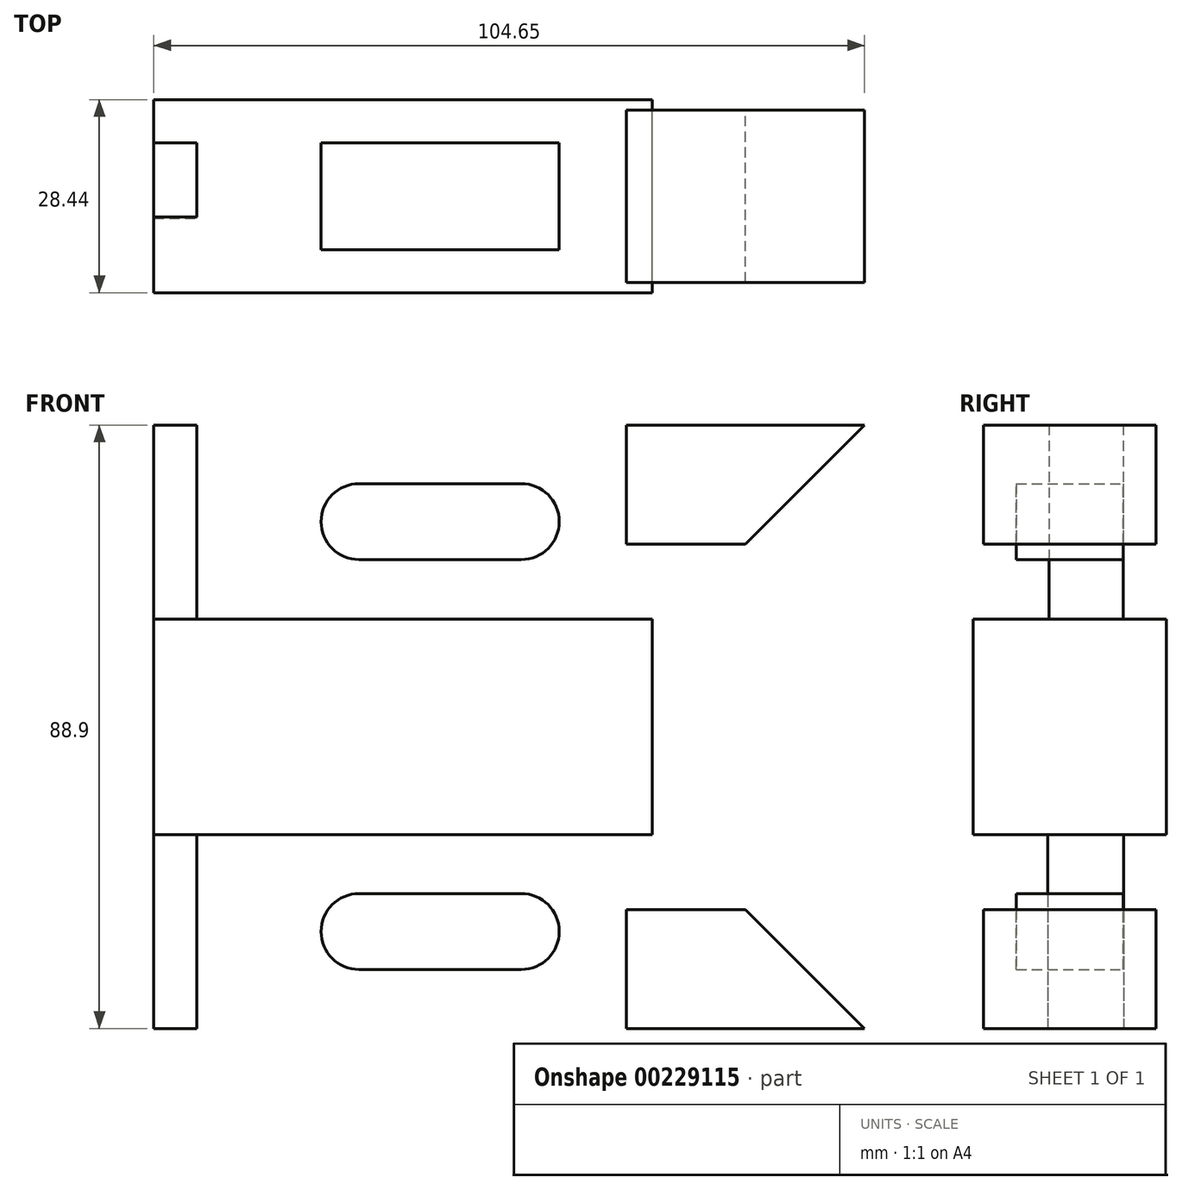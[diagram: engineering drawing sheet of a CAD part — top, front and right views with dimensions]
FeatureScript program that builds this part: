
annotation { "Feature Type Name" : "Feature", "Feature Type Description" : "" }
export const myFeature = defineFeature(function(context is Context, id is Id, definition is map)
    precondition{}
    {
        {
            var Q0;
            Q0=qCreatedBy(makeId("Front.planeOp"),FACE);
            var sketch = newSketch(context, id + "F0", { "sketchPlane" : qUnion([Q0])});
            skLineSegment(sketch, "E0.bottom", {"start": v(0, 0) * mm, "end": v(-104.65, 0) * mm});
            skLineSegment(sketch, "E0.top", {"start": v(0, 28.57) * mm, "end": v(-104.65, 28.57) * mm});
            skLineSegment(sketch, "E0.right", {"start": v(-104.65, 0) * mm, "end": v(-104.65, 28.58) * mm});
            skLineSegment(sketch, "E1", {"start": v(-74.42, 14.35) * mm, "end": v(-50.55, 14.35) * mm, "construction": true});
            skArc(sketch, "E2.0.startCap", {"start": v(-74.42, 8.76) * mm, "mid": v(-80, 14.35) * mm, "end": v(-74.42, 19.94) * mm});
            skArc(sketch, "E2.0.endCap", {"start": v(-50.55, 19.94) * mm, "mid": v(-44.96, 14.35) * mm, "end": v(-50.55, 8.76) * mm});
            skLineSegment(sketch, "E2.0.left", {"start": v(-74.42, 19.94) * mm, "end": v(-50.55, 19.94) * mm});
            skLineSegment(sketch, "E2.0.right", {"start": v(-74.42, 8.76) * mm, "end": v(-50.55, 8.76) * mm});
            skLineSegment(sketch, "E3.bottom", {"start": v(-104.65, 0) * mm, "end": v(-31.24, 0) * mm});
            skLineSegment(sketch, "E3.top", {"start": v(-104.65, -31.75) * mm, "end": v(-31.24, -31.75) * mm});
            skLineSegment(sketch, "E3.left", {"start": v(-104.65, 0) * mm, "end": v(-104.65, -31.75) * mm});
            skLineSegment(sketch, "E3.right", {"start": v(-31.24, 0) * mm, "end": v(-31.24, -31.75) * mm});
            skLineSegment(sketch, "E4.top", {"start": v(-104.65, -60.32) * mm, "end": v(0, -60.33) * mm});
            skLineSegment(sketch, "E4.left", {"start": v(-104.65, -31.75) * mm, "end": v(-104.65, -60.32) * mm});
            skLineSegment(sketch, "E5", {"start": v(-74.42, -46.04) * mm, "end": v(-50.55, -46.04) * mm, "construction": true});
            skPoint(sketch, "E5.startSnap0", {"position": v(-104.65, -46.04) * mm});
            skArc(sketch, "E6.0.startCap", {"start": v(-74.42, -51.63) * mm, "mid": v(-80, -46.04) * mm, "end": v(-74.42, -40.45) * mm});
            skArc(sketch, "E6.0.endCap", {"start": v(-50.55, -40.45) * mm, "mid": v(-44.96, -46.04) * mm, "end": v(-50.55, -51.63) * mm});
            skLineSegment(sketch, "E6.0.left", {"start": v(-74.42, -40.45) * mm, "end": v(-50.55, -40.45) * mm});
            skLineSegment(sketch, "E6.0.right", {"start": v(-74.42, -51.63) * mm, "end": v(-50.55, -51.63) * mm});
            skLineSegment(sketch, "E7", {"start": v(0, -60.32) * mm, "end": v(-28.58, -31.75) * mm});
            skLineSegment(sketch, "E8", {"start": v(0, 28.57) * mm, "end": v(-28.57, 0) * mm});
            skLineSegment(sketch, "E9", {"start": v(-31.24, 0) * mm, "end": v(-28.57, 0) * mm});
            skLineSegment(sketch, "E10", {"start": v(-31.24, -31.75) * mm, "end": v(-28.58, -31.75) * mm});
            skLineSegment(sketch, "E11", {"start": v(-98.3, 28.58) * mm, "end": v(-98.3, 0) * mm});
            skLineSegment(sketch, "E12", {"start": v(-98.3, -31.75) * mm, "end": v(-98.3, -60.32) * mm});
            skLineSegment(sketch, "E13", {"start": v(-35.05, 28.58) * mm, "end": v(-35.05, 11.05) * mm});
            skLineSegment(sketch, "E14", {"start": v(-35.05, 11.05) * mm, "end": v(-17.53, 11.05) * mm});
            skLineSegment(sketch, "E15", {"start": v(-35.05, -60.33) * mm, "end": v(-35.05, -42.8) * mm});
            skLineSegment(sketch, "E16", {"start": v(-35.05, -42.8) * mm, "end": v(-17.53, -42.8) * mm});
            skSolve(sketch);
        }
        {
            var Q0;
            {var subQ1=sQuery(id+"F0.wireOp",EDGE,"E3.left");Q0=makeQuery(id+"F0.imprint","IMPRINT",FACE,{"disambiguationData":[TD([[makeQuery(id+"F0.imprint","IMPRINT",EDGE,{"derivedFrom":subQ1}),1.0]])]});}
            extrude(context, id + "F1", {"entities" : qUnion([Q0]), "endBound" : BoundingType.SYMMETRIC, "depth" : 28.45 * mm});
        }
        {
            var Q0;
            {var subQ3=sQuery(id+"F0.wireOp",EDGE,"E13");Q0=makeQuery(id+"F0.imprint","IMPRINT",FACE,{"disambiguationData":[TD([[makeQuery(id+"F0.imprint","IMPRINT",EDGE,{"derivedFrom":subQ3}),1.0]])]});}
            var Q1;
            {var subQ3=sQuery(id+"F0.wireOp",EDGE,"E15");Q1=makeQuery(id+"F0.imprint","IMPRINT",FACE,{"disambiguationData":[TD([[makeQuery(id+"F0.imprint","IMPRINT",EDGE,{"derivedFrom":subQ3}),-1.0]])]});}
            extrude(context, id + "F2", {"entities" : qUnion([Q0, Q1]), "endBound" : BoundingType.SYMMETRIC, "depth" : 25.4 * mm});
        }
        {
            var Q0;
            Q0=makeQuery(id+"F0.imprint","IMPRINT",FACE,{"disambiguationData":[TD([[makeQuery(id+"F0.imprint","IMPRINT",EDGE,{"derivedFrom":sQuery(id+"F0.wireOp",EDGE,"E2.0.startCap")}),1.0]])]});
            var Q1;
            Q1=makeQuery(id+"F0.imprint","IMPRINT",FACE,{"disambiguationData":[TD([[makeQuery(id+"F0.imprint","IMPRINT",EDGE,{"derivedFrom":sQuery(id+"F0.wireOp",EDGE,"E6.0.startCap")}),1.0]])]});
            extrude(context, id + "F3", {"entities" : qUnion([Q0, Q1]), "endBound" : BoundingType.SYMMETRIC, "depth" : 15.75 * mm});
        }
        {
            var Q0;
            Q0=qCreatedBy(makeId("Top.planeOp"),FACE);
            var sketch = newSketch(context, id + "F4", { "sketchPlane" : qUnion([Q0])});
            skLineSegment(sketch, "E17.bottom", {"start": v(-98.3, 7.87) * mm, "end": v(-104.65, 7.87) * mm});
            skLineSegment(sketch, "E17.top", {"start": v(-98.3, -3.05) * mm, "end": v(-104.65, -3.05) * mm});
            skLineSegment(sketch, "E17.left", {"start": v(-98.3, 7.87) * mm, "end": v(-98.3, -3.05) * mm});
            skLineSegment(sketch, "E17.right", {"start": v(-104.65, 7.87) * mm, "end": v(-104.65, -3.05) * mm});
            skSolve(sketch);
        }
        {
            var Q0;
            Q0 = qSketchRegion(id + "F4", true);
            extrude(context, id + "F5", {"entities" : qUnion([Q0]), "depth" : 28.57 * mm});
        }
        {
            var Q0;
            {var subQ0=sQuery(id+"F0.wireOp",EDGE,"E4.left");Q0=makeQuery(id+"F0.imprint","IMPRINT",FACE,{"disambiguationData":[TD([[makeQuery(id+"F0.imprint","IMPRINT",EDGE,{"derivedFrom":subQ0}),1.0]])]});}
            extrude(context, id + "F6", {"entities" : qUnion([Q0]), "depth" : 3.24 * mm, "hasSecondDirection" : true, "secondDirectionOppositeDirection" : true, "secondDirectionDepth" : 7.9 * mm});
        }
    });
